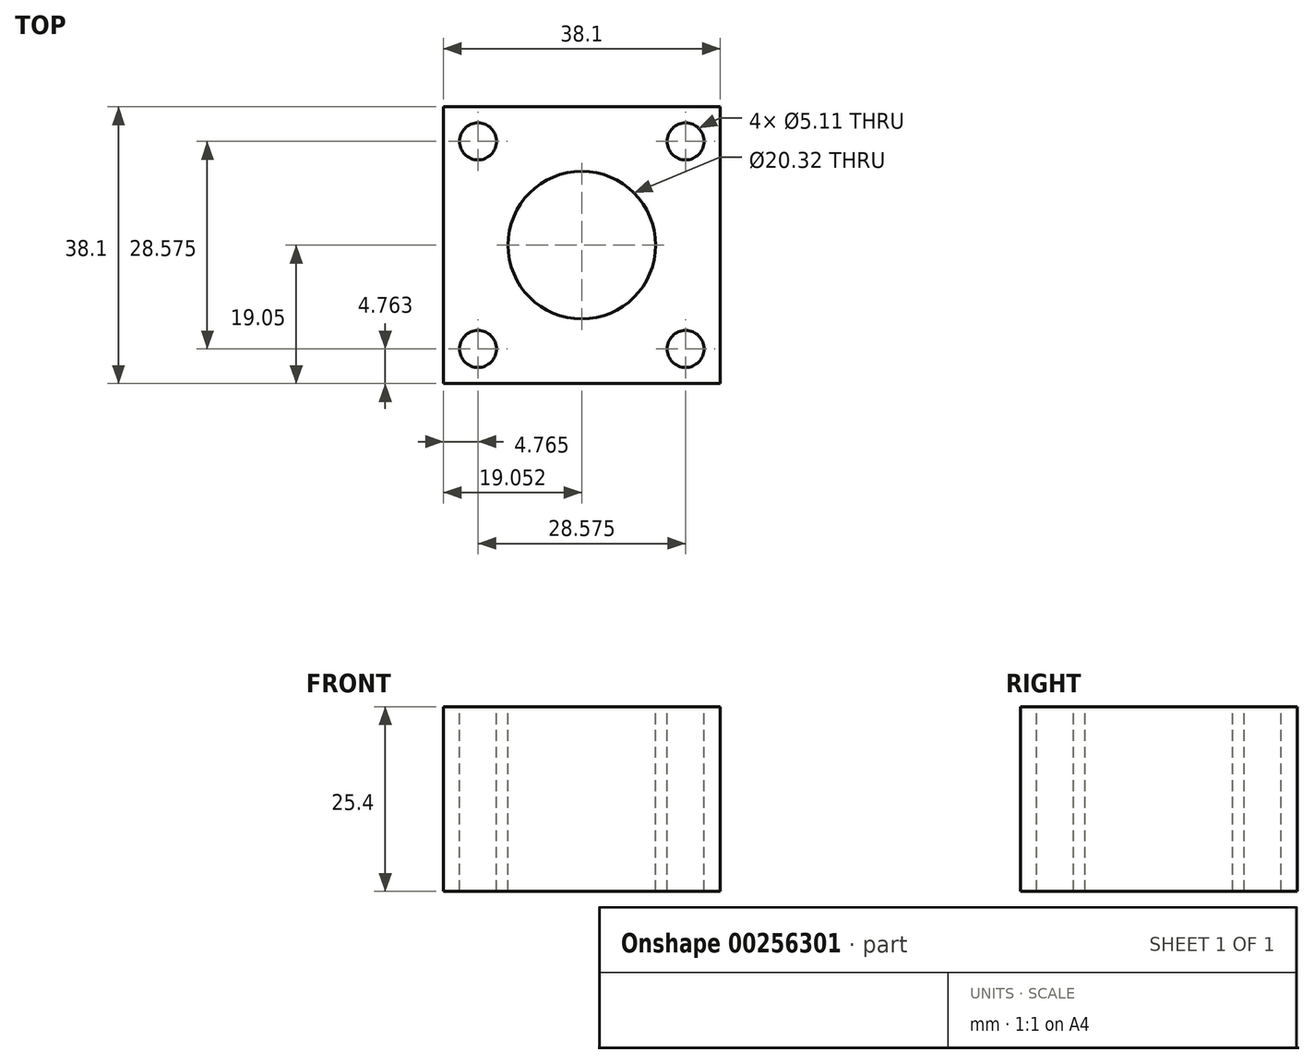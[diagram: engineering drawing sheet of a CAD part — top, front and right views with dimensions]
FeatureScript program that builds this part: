
annotation { "Feature Type Name" : "Feature", "Feature Type Description" : "" }
export const myFeature = defineFeature(function(context is Context, id is Id, definition is map)
    precondition{}
    {
        {
            var Q0;
            Q0=qCreatedBy(makeId("Top.planeOp"),FACE);
            var sketch = newSketch(context, id + "F0", { "sketchPlane" : qUnion([Q0])});
            skLineSegment(sketch, "E0.bottom", {"start": v(-47.42, 46.1) * mm, "end": v(54.18, 46.1) * mm});
            skLineSegment(sketch, "E0.top", {"start": v(-47.42, -30.1) * mm, "end": v(54.18, -30.1) * mm});
            skLineSegment(sketch, "E0.left", {"start": v(-47.42, 46.1) * mm, "end": v(-47.42, -30.1) * mm});
            skLineSegment(sketch, "E0.right", {"start": v(54.18, 46.1) * mm, "end": v(54.18, -30.1) * mm});
            skLineSegment(sketch, "E1.bottom", {"start": v(-47.42, 46.1) * mm, "end": v(-22.02, 46.1) * mm});
            skLineSegment(sketch, "E1.top", {"start": v(-47.42, 60.39) * mm, "end": v(-22.02, 60.39) * mm});
            skLineSegment(sketch, "E1.left", {"start": v(-47.42, 46.1) * mm, "end": v(-47.42, 60.39) * mm});
            skLineSegment(sketch, "E1.right", {"start": v(-22.02, 46.1) * mm, "end": v(-22.02, 60.39) * mm});
            skLineSegment(sketch, "E2.bottom", {"start": v(-47.42, -30.1) * mm, "end": v(-22.02, -30.1) * mm});
            skLineSegment(sketch, "E2.top", {"start": v(-47.42, -44.39) * mm, "end": v(-22.02, -44.39) * mm});
            skLineSegment(sketch, "E2.left", {"start": v(-47.42, -30.1) * mm, "end": v(-47.42, -44.39) * mm});
            skLineSegment(sketch, "E2.right", {"start": v(-22.02, -30.1) * mm, "end": v(-22.02, -44.39) * mm});
            skSolve(sketch);
        }
        {
            var Q0;
            {var subQ0=sQuery(id+"F0.wireOp",EDGE,"GhFNkOQN-uWCU-XlUT-uK2Q-muFrFqYSkKS1");var subQ1=sQuery(id+"F0.wireOp",EDGE,"E0.left");var subQ2=makeQuery(id+"F0.imprint","INTERSECT",VERTEX,{"disambiguationData":[OD(0.0)],"derivedFrom":[subQ1,subQ0]});Q0=makeQuery(id+"F0.imprint","IMPRINT",FACE,{"disambiguationData":[TD([[makeQuery(id+"F0.imprint","IMPRINT",EDGE,{"disambiguationData":[TD([[subQ2,-1.0]])],"derivedFrom":subQ1}),1.0]])]});}
            var Q1;
            Q1=makeQuery(id+"F0.imprint","IMPRINT",FACE,{"disambiguationData":[TD([[makeQuery(id+"F0.imprint","IMPRINT",EDGE,{"derivedFrom":sQuery(id+"F0.wireOp",EDGE,"E1.bottom")}),1.0]])]});
            var Q2;
            Q2=makeQuery(id+"F0.imprint","IMPRINT",FACE,{"disambiguationData":[TD([[makeQuery(id+"F0.imprint","IMPRINT",EDGE,{"derivedFrom":sQuery(id+"F0.wireOp",EDGE,"E0.bottom")}),-1.0]])]});
            var Q3;
            Q3=makeQuery(id+"F0.imprint","IMPRINT",FACE,{"disambiguationData":[TD([[makeQuery(id+"F0.imprint","IMPRINT",EDGE,{"derivedFrom":sQuery(id+"F0.wireOp",EDGE,"E2.bottom")}),-1.0]])]});
            extrude(context, id + "F1", {"entities" : qUnion([Q0, Q1, Q2, Q3]), "depth" : 25.4 * mm});
        }
        {
            var Q0;
            Q0=makeQuery(id+"F1.opExtrude","CAP_FACE",FACE,{"disambiguationData":[OSD([sQuery(id+"F0.wireOp",EDGE,"E0.bottom"),sQuery(id+"F0.wireOp",EDGE,"E0.top"),sQuery(id+"F0.wireOp",EDGE,"E0.left"),sQuery(id+"F0.wireOp",EDGE,"E0.right"),sQuery(id+"F0.wireOp",EDGE,"E1.top"),sQuery(id+"F0.wireOp",EDGE,"E1.left"),sQuery(id+"F0.wireOp",EDGE,"E1.right"),sQuery(id+"F0.wireOp",EDGE,"E2.top"),sQuery(id+"F0.wireOp",EDGE,"E2.left"),sQuery(id+"F0.wireOp",EDGE,"E2.right")])],"isStart":false});
            var sketch = newSketch(context, id + "F2", { "sketchPlane" : qUnion([Q0])});
            skLineSegment(sketch, "E3.bottom", {"start": v(20.84, 22.29) * mm, "end": v(49.42, 22.29) * mm});
            skLineSegment(sketch, "E3.top", {"start": v(20.84, -6.29) * mm, "end": v(49.42, -6.29) * mm});
            skLineSegment(sketch, "E3.left", {"start": v(20.84, 22.29) * mm, "end": v(20.84, -6.29) * mm});
            skLineSegment(sketch, "E3.right", {"start": v(49.42, 22.29) * mm, "end": v(49.42, -6.29) * mm});
            skCircle(sketch, "E4", {"center": v(49.42, 22.29) * mm, "radius": 2.55 * mm});
            skCircle(sketch, "E5", {"center": v(20.84, 22.29) * mm, "radius": 2.55 * mm});
            skCircle(sketch, "E6", {"center": v(20.84, -6.29) * mm, "radius": 2.55 * mm});
            skCircle(sketch, "E7", {"center": v(49.42, -6.29) * mm, "radius": 2.55 * mm});
            skCircle(sketch, "E8", {"center": v(35.13, 8) * mm, "radius": 10.16 * mm});
            skPoint(sketch, "E8.centerSnap0", {"position": v(49.42, 8) * mm});
            skPoint(sketch, "E8.centerSnap1", {"position": v(35.13, 22.29) * mm});
            skSolve(sketch);
        }
        {
            var Q0;
            Q0=makeQuery(id+"F2.imprint","IMPRINT",FACE,{"disambiguationData":[TD([[makeQuery(id+"F2.imprint","IMPRINT",EDGE,{"derivedFrom":sQuery(id+"F2.wireOp",EDGE,"E8")}),1.0]])]});
            var Q1;
            {var subQ0=sQuery(id+"F2.wireOp",EDGE,"E3.left");var subQ1=sQuery(id+"F2.wireOp",EDGE,"E3.bottom");var subQ2=makeQuery(id+"F2.imprint","INTERSECT",VERTEX,{"derivedFrom":[subQ1,subQ0]});Q1=makeQuery(id+"F2.imprint","IMPRINT",FACE,{"disambiguationData":[TD([[makeQuery(id+"F2.imprint","IMPRINT",EDGE,{"disambiguationData":[TD([[subQ2,-1.0]])],"derivedFrom":subQ1}),-1.0]])]});}
            var Q2;
            {var subQ0=sQuery(id+"F2.wireOp",EDGE,"E3.left");var subQ1=sQuery(id+"F2.wireOp",EDGE,"E3.bottom");var subQ2=makeQuery(id+"F2.imprint","INTERSECT",VERTEX,{"derivedFrom":[subQ1,subQ0]});Q2=makeQuery(id+"F2.imprint","IMPRINT",FACE,{"disambiguationData":[TD([[makeQuery(id+"F2.imprint","IMPRINT",EDGE,{"disambiguationData":[TD([[subQ2,-1.0]])],"derivedFrom":subQ1}),1.0]])]});}
            var Q3;
            {var subQ0=sQuery(id+"F2.wireOp",EDGE,"E3.right");var subQ1=sQuery(id+"F2.wireOp",EDGE,"E3.bottom");var subQ2=makeQuery(id+"F2.imprint","INTERSECT",VERTEX,{"derivedFrom":[subQ1,subQ0]});Q3=makeQuery(id+"F2.imprint","IMPRINT",FACE,{"disambiguationData":[TD([[makeQuery(id+"F2.imprint","IMPRINT",EDGE,{"disambiguationData":[TD([[subQ2,1.0]])],"derivedFrom":subQ1}),1.0]])]});}
            var Q4;
            {var subQ0=sQuery(id+"F2.wireOp",EDGE,"E3.right");var subQ1=sQuery(id+"F2.wireOp",EDGE,"E3.bottom");var subQ2=makeQuery(id+"F2.imprint","INTERSECT",VERTEX,{"derivedFrom":[subQ1,subQ0]});Q4=makeQuery(id+"F2.imprint","IMPRINT",FACE,{"disambiguationData":[TD([[makeQuery(id+"F2.imprint","IMPRINT",EDGE,{"disambiguationData":[TD([[subQ2,1.0]])],"derivedFrom":subQ1}),-1.0]])]});}
            var Q5;
            {var subQ0=sQuery(id+"F2.wireOp",EDGE,"E3.right");var subQ1=sQuery(id+"F2.wireOp",EDGE,"E3.top");var subQ2=makeQuery(id+"F2.imprint","INTERSECT",VERTEX,{"derivedFrom":[subQ1,subQ0]});Q5=makeQuery(id+"F2.imprint","IMPRINT",FACE,{"disambiguationData":[TD([[makeQuery(id+"F2.imprint","IMPRINT",EDGE,{"disambiguationData":[TD([[subQ2,1.0]])],"derivedFrom":subQ1}),1.0]])]});}
            var Q6;
            {var subQ0=sQuery(id+"F2.wireOp",EDGE,"E3.right");var subQ1=sQuery(id+"F2.wireOp",EDGE,"E3.top");var subQ2=makeQuery(id+"F2.imprint","INTERSECT",VERTEX,{"derivedFrom":[subQ1,subQ0]});Q6=makeQuery(id+"F2.imprint","IMPRINT",FACE,{"disambiguationData":[TD([[makeQuery(id+"F2.imprint","IMPRINT",EDGE,{"disambiguationData":[TD([[subQ2,1.0]])],"derivedFrom":subQ1}),-1.0]])]});}
            var Q7;
            {var subQ0=sQuery(id+"F2.wireOp",EDGE,"E3.left");var subQ1=sQuery(id+"F2.wireOp",EDGE,"E3.top");var subQ2=makeQuery(id+"F2.imprint","INTERSECT",VERTEX,{"derivedFrom":[subQ1,subQ0]});Q7=makeQuery(id+"F2.imprint","IMPRINT",FACE,{"disambiguationData":[TD([[makeQuery(id+"F2.imprint","IMPRINT",EDGE,{"disambiguationData":[TD([[subQ2,-1.0]])],"derivedFrom":subQ1}),1.0]])]});}
            var Q8;
            {var subQ0=sQuery(id+"F2.wireOp",EDGE,"E3.left");var subQ1=sQuery(id+"F2.wireOp",EDGE,"E3.top");var subQ2=makeQuery(id+"F2.imprint","INTERSECT",VERTEX,{"derivedFrom":[subQ1,subQ0]});Q8=makeQuery(id+"F2.imprint","IMPRINT",FACE,{"disambiguationData":[TD([[makeQuery(id+"F2.imprint","IMPRINT",EDGE,{"disambiguationData":[TD([[subQ2,-1.0]])],"derivedFrom":subQ1}),-1.0]])]});}
            extrude(context, id + "F3", {"entities" : qUnion([Q0, Q1, Q2, Q3, Q4, Q5, Q6, Q7, Q8]), "operationType" : NewBodyOperationType.REMOVE, "endBound" : BoundingType.THROUGH_ALL, "oppositeDirection" : true, "depth" : 25.4 * mm});
        }
        {
            var Q0;
            Q0=makeQuery(id+"F1.opExtrude","CAP_FACE",FACE,{"disambiguationData":[OSD([sQuery(id+"F0.wireOp",EDGE,"E0.bottom"),sQuery(id+"F0.wireOp",EDGE,"E0.top"),sQuery(id+"F0.wireOp",EDGE,"E0.left"),sQuery(id+"F0.wireOp",EDGE,"E0.right"),sQuery(id+"F0.wireOp",EDGE,"E1.top"),sQuery(id+"F0.wireOp",EDGE,"E1.left"),sQuery(id+"F0.wireOp",EDGE,"E1.right"),sQuery(id+"F0.wireOp",EDGE,"E2.top"),sQuery(id+"F0.wireOp",EDGE,"E2.left"),sQuery(id+"F0.wireOp",EDGE,"E2.right")])],"isStart":false});
            var sketch = newSketch(context, id + "F4", { "sketchPlane" : qUnion([Q0])});
            skLineSegment(sketch, "E9.bottom", {"start": v(54.18, -11.05) * mm, "end": v(16.08, -11.05) * mm});
            skLineSegment(sketch, "E9.top", {"start": v(54.18, 27.05) * mm, "end": v(16.08, 27.05) * mm});
            skLineSegment(sketch, "E9.left", {"start": v(54.18, -11.05) * mm, "end": v(54.18, 27.05) * mm});
            skLineSegment(sketch, "E9.right", {"start": v(16.08, -11.05) * mm, "end": v(16.08, 27.05) * mm});
            skPoint(sketch, "E10", {"position": v(35.13, 8) * mm});
            skSolve(sketch);
        }
        {
            var Q0;
            {var subQ3=sQuery(id+"F4.wireOp",EDGE,"E9.bottom");Q0=makeQuery(id+"F4.imprint","IMPRINT",FACE,{"disambiguationData":[TD([[makeQuery(id+"F4.imprint","IMPRINT",EDGE,{"derivedFrom":subQ3}),1.0]])]});}
            extrude(context, id + "F5", {"entities" : qUnion([Q0]), "operationType" : NewBodyOperationType.REMOVE, "endBound" : BoundingType.THROUGH_ALL, "oppositeDirection" : true, "depth" : 25.4 * mm});
        }
    });
